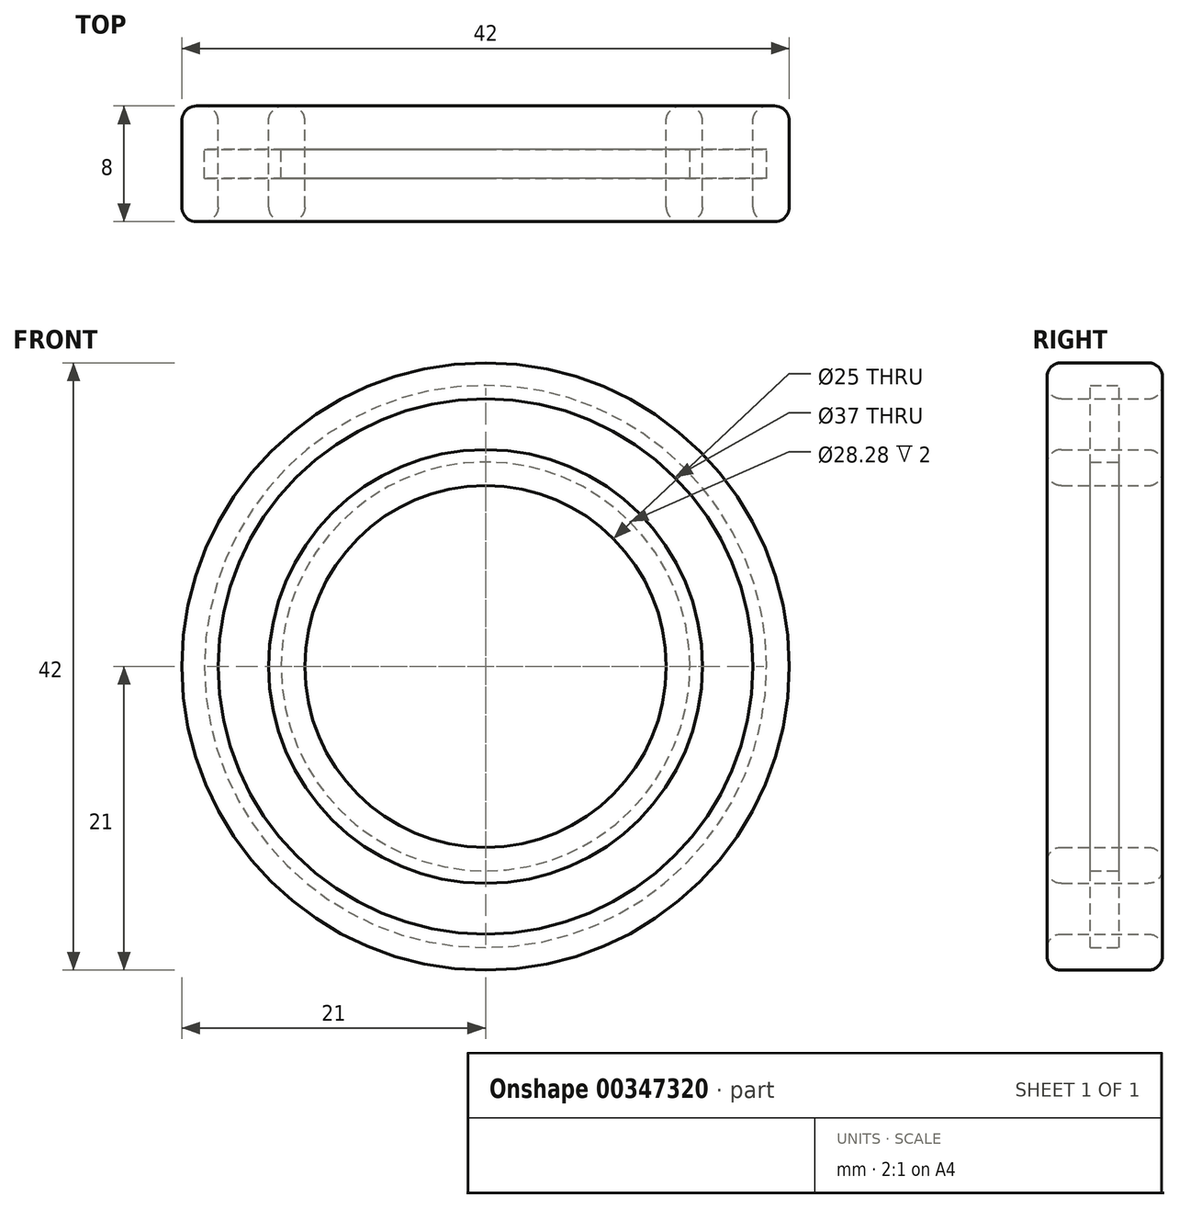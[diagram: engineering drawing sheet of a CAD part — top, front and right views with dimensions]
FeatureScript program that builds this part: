
annotation { "Feature Type Name" : "Feature", "Feature Type Description" : "" }
export const myFeature = defineFeature(function(context is Context, id is Id, definition is map)
    precondition{}
    {
        {
            var Q0;
            Q0=qCreatedBy(makeId("Front.planeOp"),FACE);
            var sketch = newSketch(context, id + "F0", { "sketchPlane" : qUnion([Q0])});
            skCircle(sketch, "E0", {"center": v(0, 0) * mm, "radius": 21 * mm});
            skCircle(sketch, "E1.0", {"center": v(0, 0) * mm, "radius": 18.5 * mm});
            skSolve(sketch);
        }
        {
            var Q0;
            Q0=makeQuery(id+"F0.imprint","IMPRINT",FACE,{"disambiguationData":[TD([[makeQuery(id+"F0.imprint","IMPRINT",EDGE,{"derivedFrom":sQuery(id+"F0.wireOp",EDGE,"E0")}),1.0]])]});
            extrude(context, id + "F1", {"entities" : qUnion([Q0]), "depth" : 4 * mm, "hasSecondDirection" : true, "secondDirectionOppositeDirection" : true, "secondDirectionDepth" : 4 * mm});
        }
        {
            var Q0;
            Q0=qCreatedBy(makeId("Front.planeOp"),FACE);
            var sketch = newSketch(context, id + "F2", { "sketchPlane" : qUnion([Q0])});
            skCircle(sketch, "E2", {"center": v(0, 0) * mm, "radius": 15 * mm});
            skCircle(sketch, "E3.0", {"center": v(0, 0) * mm, "radius": 12.5 * mm});
            skSolve(sketch);
        }
        {
            var Q0;
            Q0=makeQuery(id+"F2.imprint","IMPRINT",FACE,{"disambiguationData":[TD([[makeQuery(id+"F2.imprint","IMPRINT",EDGE,{"derivedFrom":sQuery(id+"F2.wireOp",EDGE,"E2")}),1.0]])]});
            extrude(context, id + "F3", {"entities" : qUnion([Q0]), "depth" : 4 * mm, "hasSecondDirection" : true, "secondDirectionOppositeDirection" : true, "secondDirectionDepth" : 4 * mm});
        }
        {
            var Q0;
            Q0=makeQuery(id+"F1.opExtrude","CAP_FACE",FACE,{"disambiguationData":[OSD([sQuery(id+"F0.wireOp",EDGE,"E0"),sQuery(id+"F0.wireOp",EDGE,"E1.0")])],"isStart":false});
            cPlane(context, id + "F4", {"entities" : qUnion([Q0]), "cplaneType" : CPlaneType.OFFSET, "offset" : 4 * mm, "oppositeDirection" : true, "width" : 150 * mm, "height" : 150 * mm});
        }
        {
            var Q0;
            Q0=makeQuery(id+"F1.opExtrude","CAP_EDGE",EDGE,{"disambiguationData":[OSD([sQuery(id+"F0.wireOp",EDGE,"E0")])],"isStart":false});
            var Q1;
            Q1=makeQuery(id+"F1.opExtrude","CAP_EDGE",EDGE,{"disambiguationData":[OSD([sQuery(id+"F0.wireOp",EDGE,"E0")])],"isStart":true});
            var Q2;
            Q2=makeQuery(id+"F3.opExtrude","CAP_EDGE",EDGE,{"disambiguationData":[OSD([sQuery(id+"F2.wireOp",EDGE,"E3.0")])],"isStart":false});
            var Q3;
            Q3=makeQuery(id+"F3.opExtrude","CAP_EDGE",EDGE,{"disambiguationData":[OSD([sQuery(id+"F2.wireOp",EDGE,"E2")])],"isStart":false});
            var Q4;
            Q4=makeQuery(id+"F1.opExtrude","CAP_EDGE",EDGE,{"disambiguationData":[OSD([sQuery(id+"F0.wireOp",EDGE,"E1.0")])],"isStart":true});
            var Q5;
            Q5=makeQuery(id+"F3.opExtrude","CAP_EDGE",EDGE,{"disambiguationData":[OSD([sQuery(id+"F2.wireOp",EDGE,"E3.0")])],"isStart":true});
            var Q6;
            Q6=makeQuery(id+"F3.opExtrude","CAP_EDGE",EDGE,{"disambiguationData":[OSD([sQuery(id+"F2.wireOp",EDGE,"E2")])],"isStart":true});
            var Q7;
            Q7=makeQuery(id+"F1.opExtrude","CAP_EDGE",EDGE,{"disambiguationData":[OSD([sQuery(id+"F0.wireOp",EDGE,"E1.0")])],"isStart":false});
            fillet(context, id + "F5", {"entities" : qUnion([Q0, Q1, Q2, Q3, Q4, Q5, Q6, Q7]), "radius" : 1 * mm, "tangentPropagation" : true, "allowEdgeOverflow" : false});
        }
        {
            var Q0;
            Q0=qCreatedBy(id+"F4.planeOp",FACE);
            var sketch = newSketch(context, id + "F6", { "sketchPlane" : qUnion([Q0])});
            skCircle(sketch, "E4", {"center": v(0, 0) * mm, "radius": 19.44 * mm});
            skCircle(sketch, "E5", {"center": v(0, 0) * mm, "radius": 14.14 * mm});
            skSolve(sketch);
        }
        {
            var Q0;
            Q0 = qSketchRegion(id + "F6", true);
            extrude(context, id + "F7", {"entities" : qUnion([Q0]), "depth" : 1 * mm, "hasSecondDirection" : true, "secondDirectionOppositeDirection" : true, "secondDirectionDepth" : 1 * mm});
        }
    });
